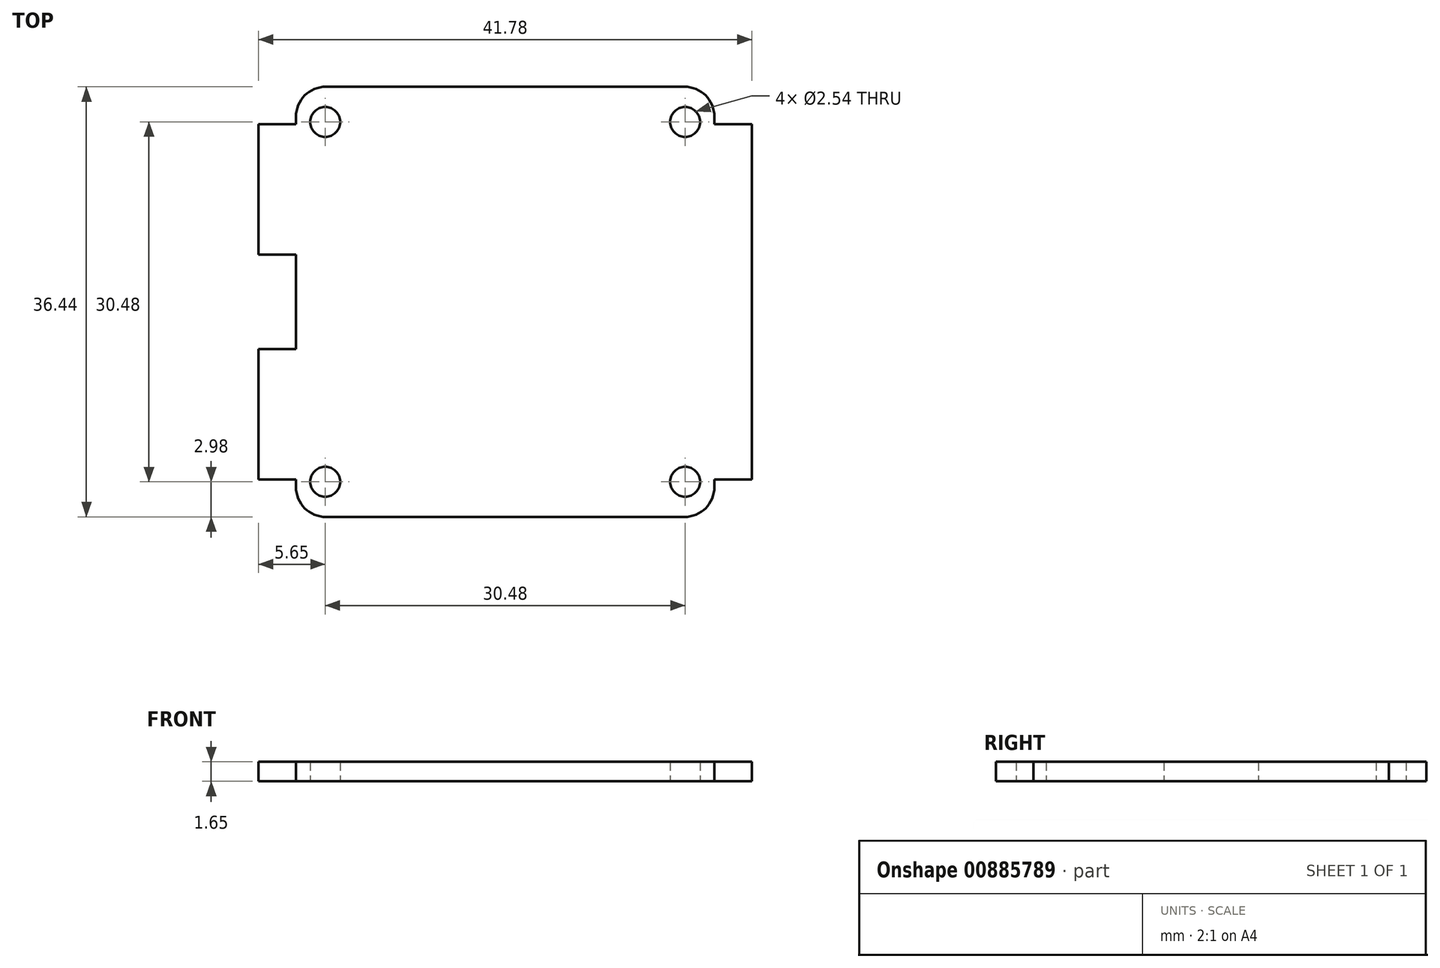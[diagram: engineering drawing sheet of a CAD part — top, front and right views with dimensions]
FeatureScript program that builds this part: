
annotation { "Feature Type Name" : "Feature", "Feature Type Description" : "" }
export const myFeature = defineFeature(function(context is Context, id is Id, definition is map)
    precondition{}
    {
        {
            var Q0;
            Q0=qCreatedBy(makeId("Top.planeOp"),FACE);
            var sketch = newSketch(context, id + "F0", { "sketchPlane" : qUnion([Q0])});
            skLineSegment(sketch, "E0.bottom", {"start": v(15.18, -18.22) * mm, "end": v(-15.18, -18.22) * mm});
            skLineSegment(sketch, "E0.top", {"start": v(15.18, 18.22) * mm, "end": v(-15.18, 18.22) * mm});
            skLineSegment(sketch, "E0.left", {"start": v(20.9, -15.05) * mm, "end": v(20.9, 15.05) * mm});
            skLineSegment(sketch, "E0.right", {"start": v(-20.9, -15.05) * mm, "end": v(-20.9, -4) * mm});
            skPoint(sketch, "E0.middle", {"position": v(0, 0) * mm});
            skLineSegment(sketch, "E1", {"start": v(-20.9, 19) * mm, "end": v(-17.72, 19) * mm, "construction": true});
            skLineSegment(sketch, "E2", {"start": v(-22.06, 18.22) * mm, "end": v(-22.06, 15.05) * mm, "construction": true});
            skLineSegment(sketch, "E3.top", {"start": v(-20.9, 15.05) * mm, "end": v(-17.72, 15.05) * mm});
            skLineSegment(sketch, "E3.right", {"start": v(-17.72, 15.68) * mm, "end": v(-17.72, 15.05) * mm});
            skPoint(sketch, "E4.orphan", {"position": v(-20.9, 18.22) * mm});
            skLineSegment(sketch, "E5", {"start": v(-21.44, -18.22) * mm, "end": v(-21.44, -15.05) * mm, "construction": true});
            skLineSegment(sketch, "E6", {"start": v(-20.9, -19.1) * mm, "end": v(-17.72, -19.1) * mm, "construction": true});
            skLineSegment(sketch, "E7.top", {"start": v(-20.9, -15.05) * mm, "end": v(-17.72, -15.05) * mm});
            skLineSegment(sketch, "E7.right", {"start": v(-17.72, -15.68) * mm, "end": v(-17.72, -15.05) * mm});
            skPoint(sketch, "E8.orphan", {"position": v(-20.9, -18.22) * mm});
            skPoint(sketch, "E9.visualSharp", {"position": v(-17.72, 18.22) * mm});
            skArc(sketch, "E9.filletArc", {"start": v(-15.18, 18.22) * mm, "mid": v(-16.97, 17.48) * mm, "end": v(-17.72, 15.68) * mm});
            skPoint(sketch, "E10.visualSharp", {"position": v(-17.72, -18.22) * mm});
            skArc(sketch, "E10.filletArc", {"start": v(-17.72, -15.68) * mm, "mid": v(-16.97, -17.48) * mm, "end": v(-15.18, -18.22) * mm});
            skLineSegment(sketch, "E11.bottom", {"start": v(-20.9, -4) * mm, "end": v(-17.72, -4) * mm});
            skLineSegment(sketch, "E11.top", {"start": v(-20.9, 4) * mm, "end": v(-17.72, 4) * mm});
            skPoint(sketch, "E11.middle", {"position": v(-17.72, 0) * mm});
            skLineSegment(sketch, "E12", {"start": v(-17.72, 4) * mm, "end": v(-17.72, -4) * mm});
            skLineSegment(sketch, "E13.trimOffspring", {"start": v(-20.9, 4) * mm, "end": v(-20.9, 15.05) * mm});
            skPoint(sketch, "E14.orphan", {"position": v(-21.94, 4) * mm});
            skPoint(sketch, "E15.orphan", {"position": v(-21.94, -4) * mm});
            skPoint(sketch, "E11.right.start.orphan", {"position": v(-13.49, -4) * mm});
            skPoint(sketch, "E16.orphan", {"position": v(-13.49, 4) * mm});
            skLineSegment(sketch, "E17", {"start": v(20.9, 0) * mm, "end": v(17.72, 0) * mm, "construction": true});
            skLineSegment(sketch, "E18", {"start": v(17.72, -15.68) * mm, "end": v(17.72, -15.05) * mm});
            skLineSegment(sketch, "E19", {"start": v(17.72, -15.05) * mm, "end": v(20.9, -15.05) * mm});
            skPoint(sketch, "E20.orphan", {"position": v(20.9, -18.22) * mm});
            skLineSegment(sketch, "E21", {"start": v(17.72, 15.68) * mm, "end": v(17.72, 15.05) * mm});
            skLineSegment(sketch, "E22", {"start": v(17.72, 15.05) * mm, "end": v(20.9, 15.05) * mm});
            skPoint(sketch, "E23.orphan", {"position": v(20.9, 18.22) * mm});
            skPoint(sketch, "E24.visualSharp", {"position": v(17.72, 18.22) * mm});
            skArc(sketch, "E24.filletArc", {"start": v(17.72, 15.68) * mm, "mid": v(16.97, 17.48) * mm, "end": v(15.18, 18.22) * mm});
            skPoint(sketch, "E25.visualSharp", {"position": v(17.72, -18.22) * mm});
            skArc(sketch, "E25.filletArc", {"start": v(15.18, -18.22) * mm, "mid": v(16.97, -17.48) * mm, "end": v(17.72, -15.68) * mm});
            skLineSegment(sketch, "E26.bottom", {"start": v(15.24, -15.24) * mm, "end": v(-15.24, -15.24) * mm, "construction": true});
            skLineSegment(sketch, "E26.top", {"start": v(15.24, 15.24) * mm, "end": v(-15.24, 15.24) * mm, "construction": true});
            skLineSegment(sketch, "E26.left", {"start": v(15.24, -15.24) * mm, "end": v(15.24, 15.24) * mm, "construction": true});
            skLineSegment(sketch, "E26.right", {"start": v(-15.24, -15.24) * mm, "end": v(-15.24, 15.24) * mm, "construction": true});
            skCircle(sketch, "E27", {"center": v(-15.24, 15.24) * mm, "radius": 1.27 * mm});
            skCircle(sketch, "E28", {"center": v(15.24, 15.24) * mm, "radius": 1.27 * mm});
            skCircle(sketch, "E29", {"center": v(15.24, -15.24) * mm, "radius": 1.27 * mm});
            skCircle(sketch, "E30", {"center": v(-15.24, -15.24) * mm, "radius": 1.27 * mm});
            skSolve(sketch);
        }
        {
            var Q0;
            Q0 = qSketchRegion(id + "F0", true);
            extrude(context, id + "F1", {"entities" : qUnion([Q0]), "depth" : 1.65 * mm, "offsetDistance" : 25.4 * mm});
        }
    });
